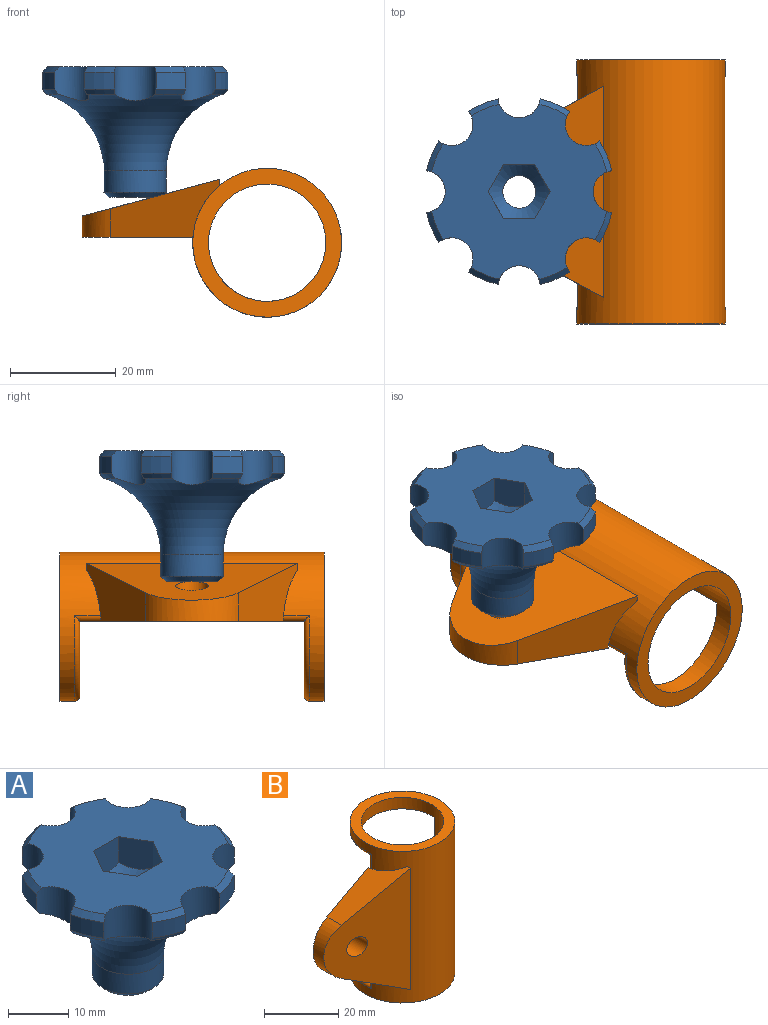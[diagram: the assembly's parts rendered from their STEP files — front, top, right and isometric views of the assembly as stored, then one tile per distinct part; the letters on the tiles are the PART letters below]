
ASSEMBLY  parts=2 mates=1
PART A: 45 faces, bbox 45.5x45.5x30.6 mm
  f0: plane 33.17x33.17mm, normal (0,0,1), area 688.8mm2, adj f2,f5,f8,f11,f14,f17,f21,f27
  f1: cone r=18mm half-angle=37.9deg, axis (0,0,1), area 7.3mm2, adj f23,f24,f36,f43
  f2: cone r=17mm half-angle=45deg, axis (0,0,-1), area 8.4mm2, adj f0,f24,f36,f43
  f3: cylinder r=18mm len=5.63mm, axis (0,0,1), area 19.6mm2, adj f4,f5,f42,f43
  f4: cone r=18mm half-angle=37.9deg, axis (0,0,1), area 7.3mm2, adj f3,f23,f42,f43
  f5: cone r=17mm half-angle=45deg, axis (0,0,-1), area 8.4mm2, adj f0,f3,f42,f43
  f6: cylinder r=18mm len=5.63mm, axis (0,0,1), area 19.6mm2, adj f7,f8,f41,f42
  f7: cone r=18mm half-angle=37.9deg, axis (0,0,1), area 7.3mm2, adj f6,f23,f41,f42
  f8: cone r=17mm half-angle=45deg, axis (0,0,-1), area 8.4mm2, adj f0,f6,f41,f42
  f9: cylinder r=18mm len=5.63mm, axis (0,0,1), area 19.6mm2, adj f10,f11,f40,f41
  f10: cone r=18mm half-angle=37.9deg, axis (0,0,1), area 7.3mm2, adj f9,f23,f40,f41
  f11: cone r=17mm half-angle=45deg, axis (0,0,-1), area 8.4mm2, adj f0,f9,f40,f41
  f12: cylinder r=18mm len=5.63mm, axis (0,0,1), area 19.6mm2, adj f13,f14,f39,f40
  f13: cone r=18mm half-angle=37.9deg, axis (0,0,1), area 7.3mm2, adj f12,f23,f39,f40
  f14: cone r=17mm half-angle=45deg, axis (0,0,-1), area 8.4mm2, adj f0,f12,f39,f40
  f15: cylinder r=18mm len=5.63mm, axis (0,0,1), area 19.6mm2, adj f16,f17,f38,f39
  f16: cone r=18mm half-angle=37.9deg, axis (0,0,1), area 7.3mm2, adj f15,f23,f38,f39
  f17: cone r=17mm half-angle=45deg, axis (0,0,-1), area 8.4mm2, adj f0,f15,f38,f39
  f18: cylinder r=18mm len=5.63mm, axis (0,0,1), area 19.6mm2, adj f20,f21,f37,f38
  f19: cylinder r=18mm len=5.63mm, axis (0,0,1), area 19.6mm2, adj f34,f35,f36,f37
  f20: cone r=18mm half-angle=37.9deg, axis (0,0,1), area 7.3mm2, adj f18,f23,f37,f38
  f21: cone r=17mm half-angle=45deg, axis (0,0,-1), area 8.4mm2, adj f0,f18,f37,f38
  f22: cylinder r=3.1mm len=16.72mm, axis (0,0,1), area 325.6mm2, adj f25,f44
  f23: torus R=20.9mm, axis (0,0,1), area 1085.1mm2, adj f1,f4,f7,f10,f13,f16,f20,f26
  f24: cylinder r=18mm len=5.63mm, axis (0,0,1), area 19.6mm2, adj f1,f2,f36,f43
  f25: plane 9.8x9.8mm, normal (0,0,-1), area 45.2mm2, adj f22,f33
  f26: cylinder r=5.9mm len=11.8mm, axis (0,0,1), area 148.3mm2, adj f23,f33
  f27: plane 6.01x5.1mm, normal (0.87,-0.5,0), area 33.7mm2, adj f0,f28,f32,f44
  f28: plane 6.01x5.1mm, normal (0.87,0.5,0), area 33.7mm2, adj f0,f27,f29,f44
  f29: plane 6.01x5.89mm, normal (0,1,0), area 33.7mm2, adj f0,f28,f30,f44
  f30: plane 6.29x5.38mm, normal (-0.87,0.5,0), area 33.7mm2, adj f0,f29,f31,f44
  f31: plane 6.01x5.1mm, normal (-0.87,-0.5,0), area 33.7mm2, adj f0,f30,f32,f44
  f32: plane 6.01x5.89mm, normal (0,-1,0), area 33.7mm2, adj f0,f27,f31,f44
  f33: cone r=5.9mm half-angle=45deg, axis (0,0,1), area 48mm2, adj f25,f26
  f34: cone r=18mm half-angle=37.9deg, axis (0,0,1), area 7.3mm2, adj f19,f23,f36,f37
  f35: cone r=17mm half-angle=45deg, axis (0,0,-1), area 8.4mm2, adj f0,f19,f36,f37
  f36: cylinder r=4mm len=7.95mm, axis (0,0,1), area 65.9mm2, adj f0,f1,f2,f19,f23,f24,f34,f35
  f37: cylinder r=4mm len=6.5mm, axis (0,0,1), area 65.9mm2, adj f0,f18,f19,f20,f21,f23,f34,f35
  f38: cylinder r=4mm len=7.95mm, axis (0,0,1), area 65.9mm2, adj f0,f15,f16,f17,f18,f20,f21,f23
  f39: cylinder r=4mm len=6.5mm, axis (0,0,1), area 65.9mm2, adj f0,f12,f13,f14,f15,f16,f17,f23
  f40: cylinder r=4mm len=7.95mm, axis (0,0,1), area 64.9mm2, adj f0,f9,f10,f11,f12,f13,f14,f23
  f41: cylinder r=4mm len=6.5mm, axis (0,0,1), area 65.9mm2, adj f0,f6,f7,f8,f9,f10,f11,f23
  f42: cylinder r=4mm len=7.95mm, axis (0,0,1), area 65.9mm2, adj f0,f3,f4,f5,f6,f7,f8,f23
  f43: cylinder r=4mm len=6.5mm, axis (0,0,1), area 65.9mm2, adj f0,f1,f2,f3,f4,f5,f23,f24
  f44: cone r=3.1mm half-angle=45deg, axis (0,0,1), area 84.9mm2, adj f22,f27,f28,f29,f30,f31,f32
PART B: 20 faces, bbox 50.6x29.7x50.3 mm
  f0: cylinder r=14.1mm len=50mm, axis (0,0,-1), area 1892.1mm2, adj f1,f2,f8,f9,f10,f11,f12,f13
  f1: plane 28.2x28.2mm, normal (0,0,-1), area 237.5mm2, adj f0,f3
  f2: plane 28.2x28.2mm, normal (0,0,1), area 237.5mm2, adj f0,f3
  f3: cylinder r=11.1mm len=50mm, axis (0,0,-1), area 1921.5mm2, adj f1,f2,f4,f5,f6,f7
  f4: plane 26.2x14.11mm, normal (0,0,1), area 80mm2, adj f3,f6,f7,f8,f10,f11
  f5: plane 26.2x14.11mm, normal (0,0,-1), area 80mm2, adj f3,f6,f7,f8,f9,f11
  f6: plane 42.46x1.89mm, normal (0,1,0), area 80.3mm2, adj f3,f4,f5,f11
  f7: plane 42.46x1.89mm, normal (0,1,0), area 80.3mm2, adj f3,f4,f5,f8
  f8: cylinder r=1mm len=44.46mm, axis (0,0,-1), area 74.4mm2, adj f0,f4,f5,f7,f9,f10
  f9: torus R=13.1mm, axis (0,0,1), area 72.8mm2, adj f0,f5,f8,f11
  f10: torus R=13.1mm, axis (0,0,-1), area 72.8mm2, adj f0,f4,f8,f11
  f11: cylinder r=1mm len=44.46mm, axis (0,0,-1), area 74.4mm2, adj f0,f4,f5,f6,f9,f10,f18
  f12: plane 40x1.15mm, normal (1,0,0), area 45.8mm2, adj f0,f13,f15,f17
  f13: plane 20.76x11.21mm, normal (-0.47,0,0.88), area 155.9mm2, adj f0,f12,f14,f17,f18,f19
  f14: cylinder r=10mm len=17.6mm, axis (0,1,0), area 97.3mm2, adj f13,f15,f17,f19
  f15: plane 20.76x11.21mm, normal (-0.47,0,-0.88), area 155.9mm2, adj f0,f12,f14,f17,f18,f19
  f16: cylinder r=3.1mm len=7.55mm, axis (0,1,0), area 131.3mm2, adj f17,f19
  f17: plane 40.35x26.35mm, normal (-0.26,-0.97,0), area 655.5mm2, adj f12,f13,f14,f15,f16
  f18: cylinder r=14.1mm len=34.67mm, axis (0,0,-1), area 40.1mm2, adj f11,f13,f15,f19
  f19: plane 34.53x20.94mm, normal (0,1,0), area 444.5mm2, adj f13,f14,f15,f16,f18
PLACE A t=(-39.83,-41.45,3.14)mm
PLACE B rot(axis=(-1,0,0),90deg) t=(-14.83,-41.45,-5.45)mm
MATE revolute B.f16 <-> A.f1  axis (0,0,-1) through (-39.83,-41.45,3.14)mm
